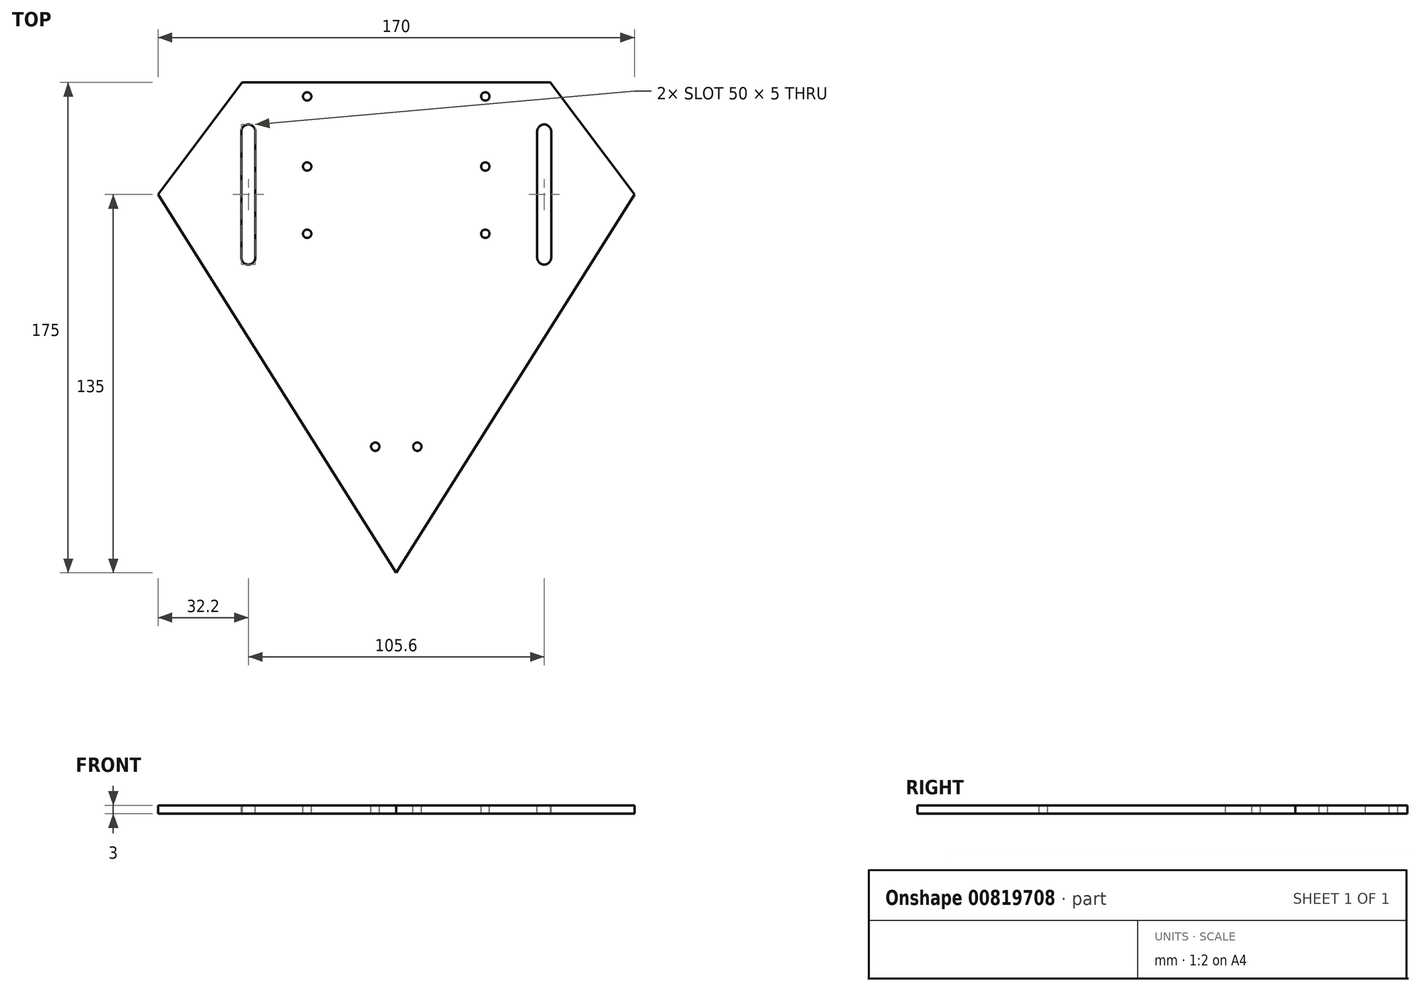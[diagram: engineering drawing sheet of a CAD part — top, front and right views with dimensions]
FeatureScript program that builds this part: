
annotation { "Feature Type Name" : "Feature", "Feature Type Description" : "" }
export const myFeature = defineFeature(function(context is Context, id is Id, definition is map)
    precondition{}
    {
        {
            var Q0;
            Q0=qCreatedBy(makeId("Top.planeOp"),FACE);
            var sketch = newSketch(context, id + "F0", { "sketchPlane" : qUnion([Q0])});
            skLineSegment(sketch, "E0", {"start": v(0, 0) * mm, "end": v(55, 0) * mm});
            skLineSegment(sketch, "E1", {"start": v(55, 0) * mm, "end": v(85, -40) * mm});
            skLineSegment(sketch, "E2", {"start": v(85, -40) * mm, "end": v(0, -175) * mm});
            skLineSegment(sketch, "E3", {"start": v(0, -175) * mm, "end": v(0, 0) * mm});
            skLineSegment(sketch, "E4", {"start": v(0, -143.14) * mm, "end": v(20.06, -143.14) * mm});
            skSolve(sketch);
        }
        {
            var Q0;
            Q0 = qSketchRegion(id + "F0", true);
            extrude(context, id + "F1", {"entities" : qUnion([Q0]), "depth" : 3 * mm, "offsetDistance" : 25.4 * mm});
        }
        {
            var Q0;
            Q0=makeQuery(id+"F1.opExtrude","CAP_FACE",FACE,{"disambiguationData":[OSD([sQuery(id+"F0.wireOp",EDGE,"E0"),sQuery(id+"F0.wireOp",EDGE,"E1"),sQuery(id+"F0.wireOp",EDGE,"E2"),sQuery(id+"F0.wireOp",EDGE,"E3")])],"isStart":false});
            var sketch = newSketch(context, id + "F2", { "sketchPlane" : qUnion([Q0])});
            skSolve(sketch);
        }
        {
            var Q0;
            Q0=makeQuery(id+"F2.imprint","IMPRINT",FACE,{"disambiguationData":[TD([[makeQuery(id+"F2.imprint","IMPRINT",EDGE,{"derivedFrom":makeQuery(id+"F1.opExtrude","CAP_EDGE",EDGE,{"disambiguationData":[OSD([sQuery(id+"F0.wireOp",EDGE,"E0")])],"isStart":false})}),-1.0]])]});
            var sketch = newSketch(context, id + "F3", { "sketchPlane" : qUnion([Q0])});
            skLineSegment(sketch, "E5", {"start": v(7.5, -130) * mm, "end": v(7.5, -130.11) * mm});
            skSolve(sketch);
        }
        {
            var Q0;
            Q0=sQuery(id+"F3.wireOp",VERTEX,"E5.start");
            var Q1;
            Q1=makeQuery(id+"F1.opExtrude","SWEPT_BODY",BODY,{"disambiguationData":[OSD([sQuery(id+"F0.wireOp",EDGE,"E0"),sQuery(id+"F0.wireOp",EDGE,"E1"),sQuery(id+"F0.wireOp",EDGE,"E2"),sQuery(id+"F0.wireOp",EDGE,"E3")])]});
            hole(context, id + "F4", {"style" : HoleStyle.SIMPLE, "endStyle" : HoleEndStyle.THROUGH, "holeDiameter" : 3 * mm, "majorDiameter" : 5 * mm, "isTappedThrough" : true, "tappedDepth" : 12 * mm, "tapClearance" : 3, "locations" : qUnion([Q0]), "scope" : qUnion([Q1])});
        }
        {
            var Q0;
            Q0=makeQuery(id+"F2.imprint","IMPRINT",FACE,{"disambiguationData":[TD([[makeQuery(id+"F2.imprint","IMPRINT",EDGE,{"derivedFrom":makeQuery(id+"F1.opExtrude","CAP_EDGE",EDGE,{"disambiguationData":[OSD([sQuery(id+"F0.wireOp",EDGE,"E0")])],"isStart":false})}),-1.0]])]});
            var sketch = newSketch(context, id + "F5", { "sketchPlane" : qUnion([Q0])});
            skLineSegment(sketch, "E6", {"start": v(31.8, -30) * mm, "end": v(31.8, -54) * mm});
            skLineSegment(sketch, "E7", {"start": v(31.8, -30) * mm, "end": v(31.8, -5) * mm});
            skSolve(sketch);
        }
        {
            var Q0;
            Q0=sQuery(id+"F5.wireOp",VERTEX,"E6.start");
            var Q1;
            Q1=sQuery(id+"F5.wireOp",VERTEX,"E6.end");
            var Q2;
            Q2=sQuery(id+"F5.wireOp",VERTEX,"E7.end");
            var Q3;
            Q3=makeQuery(id+"F1.opExtrude","SWEPT_BODY",BODY,{"disambiguationData":[OSD([sQuery(id+"F0.wireOp",EDGE,"E0"),sQuery(id+"F0.wireOp",EDGE,"E1"),sQuery(id+"F0.wireOp",EDGE,"E2"),sQuery(id+"F0.wireOp",EDGE,"E3")])]});
            hole(context, id + "F6", {"style" : HoleStyle.SIMPLE, "endStyle" : HoleEndStyle.THROUGH, "holeDiameter" : 3 * mm, "majorDiameter" : 5 * mm, "isTappedThrough" : true, "tappedDepth" : 12 * mm, "tapClearance" : 3, "locations" : qUnion([Q0, Q1, Q2]), "scope" : qUnion([Q3])});
        }
        {
            var Q0;
            Q0=makeQuery(id+"F2.imprint","IMPRINT",FACE,{"disambiguationData":[TD([[makeQuery(id+"F2.imprint","IMPRINT",EDGE,{"derivedFrom":makeQuery(id+"F1.opExtrude","CAP_EDGE",EDGE,{"disambiguationData":[OSD([sQuery(id+"F0.wireOp",EDGE,"E0")])],"isStart":false})}),-1.0]])]});
            var sketch = newSketch(context, id + "F7", { "sketchPlane" : qUnion([Q0])});
            skLineSegment(sketch, "E8", {"start": v(67.79, -12.02) * mm, "end": v(67.79, 0) * mm});
            skLineSegment(sketch, "E9", {"start": v(67.73, -17.53) * mm, "end": v(67.73, -42.53) * mm});
            skLineSegment(sketch, "E10", {"start": v(52.26, 65.2) * mm, "end": v(52.26, 65.07) * mm});
            skLineSegment(sketch, "E11", {"start": v(90.25, -55.2) * mm, "end": v(0, -55.2) * mm});
            skLineSegment(sketch, "E12", {"start": v(0, 6.77) * mm, "end": v(0, 6.77) * mm});
            skLineSegment(sketch, "E13", {"start": v(125.71, 27.8) * mm, "end": v(125.71, -2.2) * mm});
            skSolve(sketch);
        }
        {
            var Q0;
            {var subQ0=makeQuery(id+"F2.imprint","IMPRINT",EDGE,{"derivedFrom":makeQuery(id+"F1.opExtrude","CAP_EDGE",EDGE,{"disambiguationData":[OSD([sQuery(id+"F0.wireOp",EDGE,"E2")])],"isStart":false})});Q0=makeQuery(id+"F7.imprint","IMPRINT",FACE,{"disambiguationData":[TD([[makeQuery(id+"F7.imprint","IMPRINT",EDGE,{"derivedFrom":subQ0}),-1.0]])]});}
            var sketch = newSketch(context, id + "F8", { "sketchPlane" : qUnion([Q0])});
            skLineSegment(sketch, "E14", {"start": v(52.8, -17.5) * mm, "end": v(52.8, -62.5) * mm});
            skArc(sketch, "E15.0.startCap", {"start": v(50.3, -17.5) * mm, "mid": v(52.8, -15) * mm, "end": v(55.3, -17.5) * mm});
            skArc(sketch, "E15.0.endCap", {"start": v(55.3, -62.5) * mm, "mid": v(52.8, -65) * mm, "end": v(50.3, -62.5) * mm});
            skLineSegment(sketch, "E15.0.left", {"start": v(55.3, -17.5) * mm, "end": v(55.3, -62.5) * mm});
            skLineSegment(sketch, "E15.0.right", {"start": v(50.3, -17.5) * mm, "end": v(50.3, -62.5) * mm});
            skSolve(sketch);
        }
        {
            var Q0;
            Q0 = qSketchRegion(id + "F8", true);
            extrude(context, id + "F9", {"entities" : qUnion([Q0]), "operationType" : NewBodyOperationType.REMOVE, "oppositeDirection" : true, "depth" : 34.37 * mm, "offsetDistance" : 25 * mm});
        }
        {
            var Q0;
            Q0=makeQuery(id+"F1.opExtrude","SWEPT_BODY",BODY,{"disambiguationData":[OSD([sQuery(id+"F0.wireOp",EDGE,"E0"),sQuery(id+"F0.wireOp",EDGE,"E1"),sQuery(id+"F0.wireOp",EDGE,"E2"),sQuery(id+"F0.wireOp",EDGE,"E3")])]});
            var Q1;
            Q1=qCreatedBy(makeId("Right.planeOp"),FACE);
            mirror(context, id + "F10", {"operationType" : NewBodyOperationType.ADD, "entities" : qUnion([Q0]), "mirrorPlane" : qUnion([Q1])});
        }
    });
